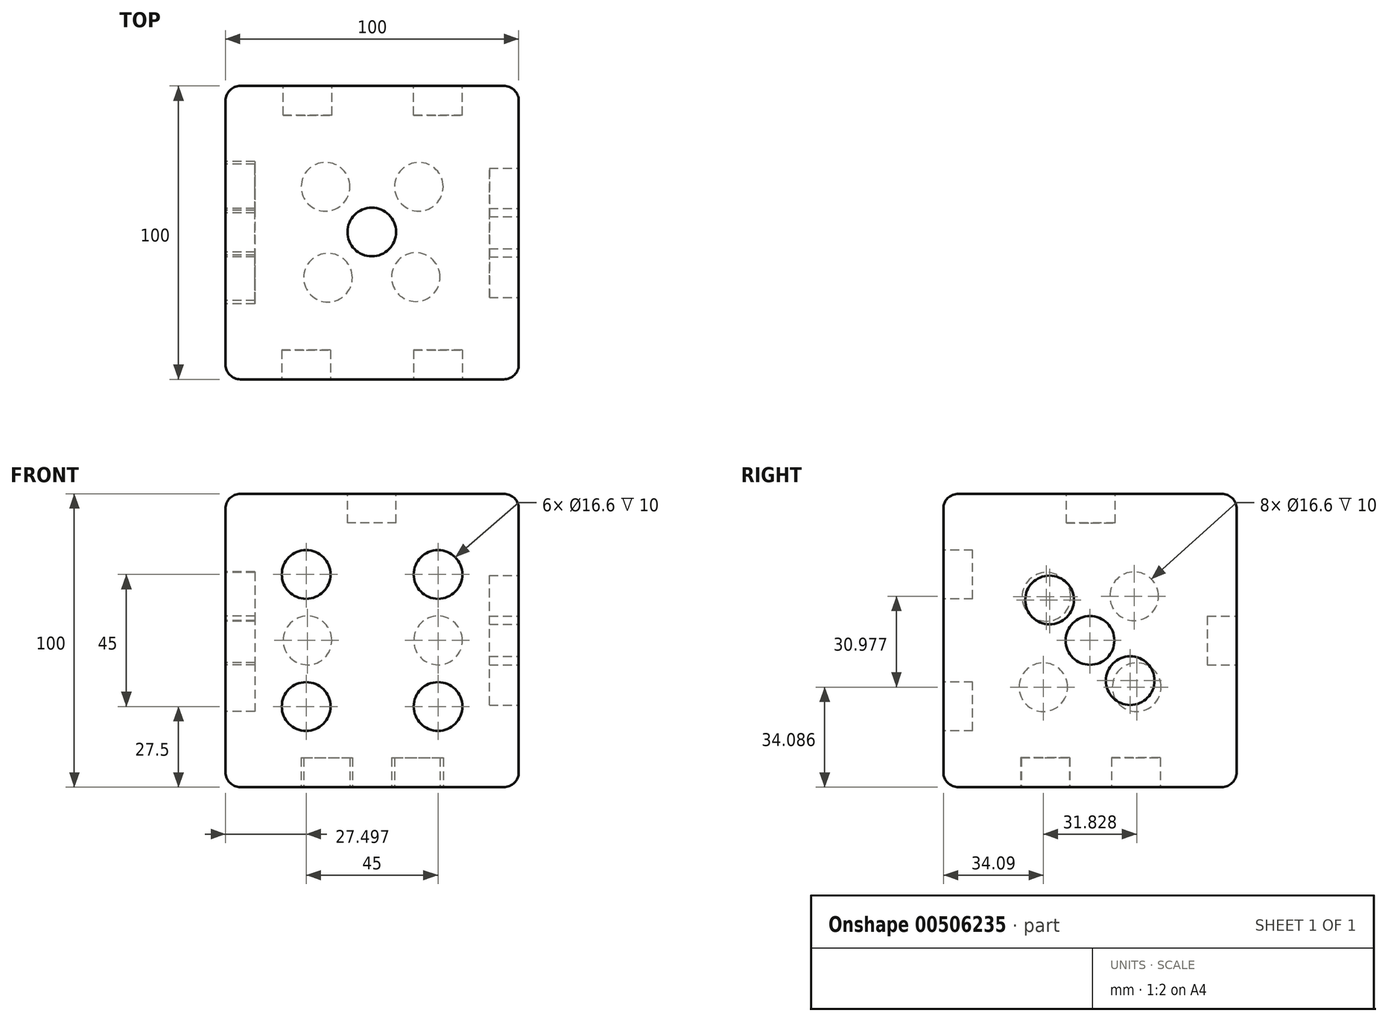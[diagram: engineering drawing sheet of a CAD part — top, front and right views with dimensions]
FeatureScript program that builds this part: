
annotation { "Feature Type Name" : "Feature", "Feature Type Description" : "" }
export const myFeature = defineFeature(function(context is Context, id is Id, definition is map)
    precondition{}
    {
        {
            var Q0;
            Q0=qCreatedBy(makeId("Top.planeOp"),FACE);
            var sketch = newSketch(context, id + "F0", { "sketchPlane" : qUnion([Q0])});
            skLineSegment(sketch, "E0.bottom", {"start": v(-61.95, 62.53) * mm, "end": v(38.05, 62.53) * mm});
            skLineSegment(sketch, "E0.top", {"start": v(-61.95, -37.47) * mm, "end": v(38.05, -37.47) * mm});
            skLineSegment(sketch, "E0.left", {"start": v(-61.95, 62.53) * mm, "end": v(-61.95, -37.47) * mm});
            skLineSegment(sketch, "E0.right", {"start": v(38.05, 62.53) * mm, "end": v(38.05, -37.47) * mm});
            skSolve(sketch);
        }
        {
            var Q0;
            Q0=makeQuery(id+"F0.imprint","IMPRINT",FACE,{"disambiguationData":[TD([[makeQuery(id+"F0.imprint","IMPRINT",EDGE,{"derivedFrom":sQuery(id+"F0.wireOp",EDGE,"E0.bottom")}),-1.0]])]});
            extrude(context, id + "F1", {"entities" : qUnion([Q0]), "depth" : 100 * mm, "offsetDistance" : 25 * mm});
        }
        {
            var Q0;
            Q0=makeQuery(id+"F1.opExtrude","CAP_EDGE",EDGE,{"disambiguationData":[OSD([sQuery(id+"F0.wireOp",EDGE,"E0.top")])],"isStart":false});
            fillet(context, id + "F2", {"entities" : qUnion([Q0]), "radius" : 5.08 * mm, "tangentPropagation" : true, "allowEdgeOverflow" : false});
        }
        {
            var Q0;
            Q0=makeQuery(id+"F1.opExtrude","CAP_EDGE",EDGE,{"disambiguationData":[OSD([sQuery(id+"F0.wireOp",EDGE,"E0.top")])],"isStart":true});
            var Q1;
            Q1=makeQuery(id+"F1.opExtrude","SWEPT_EDGE",EDGE,{"disambiguationData":[OSD([sQuery(id+"F0.wireOp",EDGE,"E0.top"),sQuery(id+"F0.wireOp",EDGE,"E0.right")])]});
            var Q2;
            Q2=makeQuery(id+"F1.opExtrude","SWEPT_EDGE",EDGE,{"disambiguationData":[OSD([sQuery(id+"F0.wireOp",EDGE,"E0.top"),sQuery(id+"F0.wireOp",EDGE,"E0.left")])]});
            var Q3;
            Q3=makeQuery(id+"F1.opExtrude","CAP_EDGE",EDGE,{"disambiguationData":[OSD([sQuery(id+"F0.wireOp",EDGE,"E0.bottom")])],"isStart":false});
            var Q4;
            Q4=makeQuery(id+"F1.opExtrude","CAP_EDGE",EDGE,{"disambiguationData":[OSD([sQuery(id+"F0.wireOp",EDGE,"E0.left")])],"isStart":false});
            var Q5;
            Q5=makeQuery(id+"F1.opExtrude","CAP_EDGE",EDGE,{"disambiguationData":[OSD([sQuery(id+"F0.wireOp",EDGE,"E0.right")])],"isStart":false});
            var Q6;
            Q6=makeQuery(id+"F1.opExtrude","CAP_EDGE",EDGE,{"disambiguationData":[OSD([sQuery(id+"F0.wireOp",EDGE,"E0.right")])],"isStart":true});
            var Q7;
            Q7=makeQuery(id+"F1.opExtrude","SWEPT_EDGE",EDGE,{"disambiguationData":[OSD([sQuery(id+"F0.wireOp",EDGE,"E0.bottom"),sQuery(id+"F0.wireOp",EDGE,"E0.right")])]});
            fillet(context, id + "F3", {"entities" : qUnion([Q0, Q1, Q2, Q3, Q4, Q5, Q6, Q7]), "radius" : 5.08 * mm, "tangentPropagation" : true, "allowEdgeOverflow" : false});
        }
        {
            var Q0;
            Q0=makeQuery(id+"F1.opExtrude","CAP_EDGE",EDGE,{"disambiguationData":[OSD([sQuery(id+"F0.wireOp",EDGE,"E0.bottom")])],"isStart":true});
            var Q1;
            Q1=makeQuery(id+"F1.opExtrude","CAP_EDGE",EDGE,{"disambiguationData":[OSD([sQuery(id+"F0.wireOp",EDGE,"E0.left")])],"isStart":true});
            var Q2;
            {var subQ0=sQuery(id+"F0.wireOp",EDGE,"E0.top");Q2=makeQuery(id+"F3.opFillet","BLEND_EDGE",EDGE,{"blendedFrom":[makeQuery(id+"F1.opExtrude","CAP_EDGE",EDGE,{"disambiguationData":[OSD([subQ0])],"isStart":true}),makeQuery(id+"F1.opExtrude","CAP_FACE",FACE,{"disambiguationData":[OSD([sQuery(id+"F0.wireOp",EDGE,"E0.bottom"),subQ0,sQuery(id+"F0.wireOp",EDGE,"E0.left"),sQuery(id+"F0.wireOp",EDGE,"E0.right")])],"isStart":true})],"blendedInto":[makeQuery(id+"F1.opExtrude","CAP_FACE",FACE,{"disambiguationData":[OSD([sQuery(id+"F0.wireOp",EDGE,"E0.bottom"),subQ0,sQuery(id+"F0.wireOp",EDGE,"E0.left"),sQuery(id+"F0.wireOp",EDGE,"E0.right")])],"isStart":true})]});}
            var Q3;
            {var subQ0=sQuery(id+"F0.wireOp",EDGE,"E0.right");Q3=makeQuery(id+"F3.opFillet","BLEND_EDGE",EDGE,{"blendedFrom":[makeQuery(id+"F1.opExtrude","CAP_EDGE",EDGE,{"disambiguationData":[OSD([subQ0])],"isStart":true}),makeQuery(id+"F1.opExtrude","CAP_FACE",FACE,{"disambiguationData":[OSD([sQuery(id+"F0.wireOp",EDGE,"E0.bottom"),sQuery(id+"F0.wireOp",EDGE,"E0.top"),sQuery(id+"F0.wireOp",EDGE,"E0.left"),subQ0])],"isStart":true})],"blendedInto":[makeQuery(id+"F1.opExtrude","CAP_FACE",FACE,{"disambiguationData":[OSD([sQuery(id+"F0.wireOp",EDGE,"E0.bottom"),sQuery(id+"F0.wireOp",EDGE,"E0.top"),sQuery(id+"F0.wireOp",EDGE,"E0.left"),subQ0])],"isStart":true})]});}
            fillet(context, id + "F4", {"entities" : qUnion([Q0, Q1, Q2, Q3]), "radius" : 5.08 * mm, "tangentPropagation" : true, "allowEdgeOverflow" : false});
        }
        {
            var Q0;
            Q0=makeQuery(id+"F1.opExtrude","SWEPT_EDGE",EDGE,{"disambiguationData":[OSD([sQuery(id+"F0.wireOp",EDGE,"E0.bottom"),sQuery(id+"F0.wireOp",EDGE,"E0.left")])]});
            fillet(context, id + "F5", {"entities" : qUnion([Q0]), "radius" : 5.08 * mm, "tangentPropagation" : true, "allowEdgeOverflow" : false});
        }
        {
            var Q0;
            Q0=makeQuery(id+"F1.opExtrude","CAP_FACE",FACE,{"disambiguationData":[OSD([sQuery(id+"F0.wireOp",EDGE,"E0.bottom"),sQuery(id+"F0.wireOp",EDGE,"E0.top"),sQuery(id+"F0.wireOp",EDGE,"E0.left"),sQuery(id+"F0.wireOp",EDGE,"E0.right")])],"isStart":false});
            var sketch = newSketch(context, id + "F6", { "sketchPlane" : qUnion([Q0])});
            skLineSegment(sketch, "E1", {"start": v(-56.87, 12.53) * mm, "end": v(32.97, 12.53) * mm});
            skLineSegment(sketch, "E2", {"start": v(-11.95, -32.39) * mm, "end": v(-11.95, 57.45) * mm});
            skSolve(sketch);
        }
        {
            var Q0;
            {var subQ0=sQuery(id+"F6.wireOp",EDGE,"E1");var subQ6=sQuery(id+"F6.wireOp",EDGE,"E2");var subQ7=makeQuery(id+"F6.imprint","INTERSECT",VERTEX,{"derivedFrom":[subQ0,subQ6]});Q0=makeQuery(id+"F6.imprint","IMPRINT",FACE,{"disambiguationData":[TD([[makeQuery(id+"F6.imprint","IMPRINT",EDGE,{"disambiguationData":[TD([[subQ7,1.0]])],"derivedFrom":subQ0}),1.0]])]});}
            var sketch = newSketch(context, id + "F7", { "sketchPlane" : qUnion([Q0])});
            skCircle(sketch, "E3", {"center": v(-12.05, 12.77) * mm, "radius": 8.3 * mm});
            skSolve(sketch);
        }
        {
            var Q0;
            {var subQ0=sQuery(id+"F7.wireOp",EDGE,"E3");var subQ1=sQuery(id+"F6.wireOp",EDGE,"E1");var subQ5=sQuery(id+"F6.wireOp",EDGE,"E2");var subQ6=makeQuery(id+"F6.imprint","INTERSECT",VERTEX,{"derivedFrom":[subQ1,subQ5]});var subQ7=makeQuery(id+"F6.imprint","IMPRINT",EDGE,{"disambiguationData":[TD([[subQ6,1.0]])],"derivedFrom":subQ1});var subQ8=makeQuery(id+"F7.imprint","INTERSECT",VERTEX,{"derivedFrom":[subQ7,subQ0]});Q0=makeQuery(id+"F7.imprint","IMPRINT",FACE,{"disambiguationData":[TD([[makeQuery(id+"F7.imprint","IMPRINT",EDGE,{"disambiguationData":[TD([[subQ8,1.0]])],"derivedFrom":subQ0}),1.0]])]});}
            var Q1;
            {var subQ0=sQuery(id+"F7.wireOp",EDGE,"E3");var subQ1=sQuery(id+"F6.wireOp",EDGE,"E1");var subQ5=sQuery(id+"F6.wireOp",EDGE,"E2");var subQ6=makeQuery(id+"F6.imprint","INTERSECT",VERTEX,{"derivedFrom":[subQ1,subQ5]});var subQ7=makeQuery(id+"F6.imprint","IMPRINT",EDGE,{"disambiguationData":[TD([[subQ6,1.0]])],"derivedFrom":subQ1});var subQ8=makeQuery(id+"F7.imprint","INTERSECT",VERTEX,{"derivedFrom":[subQ7,subQ0]});Q1=makeQuery(id+"F7.imprint","IMPRINT",FACE,{"disambiguationData":[TD([[makeQuery(id+"F7.imprint","IMPRINT",EDGE,{"disambiguationData":[TD([[subQ8,-1.0]])],"derivedFrom":subQ0}),1.0]])]});}
            var Q2;
            Q2=sQuery(id+"F7.wireOp",EDGE,"E3");
            extrude(context, id + "F8", {"entities" : qUnion([Q0, Q1]), "operationType" : NewBodyOperationType.REMOVE, "surfaceEntities" : qUnion([Q2]), "oppositeDirection" : true, "depth" : 10 * mm, "offsetDistance" : 25 * mm});
        }
        {
            var Q0;
            Q0=makeQuery(id+"F1.opExtrude","SWEPT_FACE",FACE,{"disambiguationData":[OSD([sQuery(id+"F0.wireOp",EDGE,"E0.left")])]});
            var sketch = newSketch(context, id + "F9", { "sketchPlane" : qUnion([Q0])});
            skCircle(sketch, "E4", {"center": v(-27.6, 65.06) * mm, "radius": 8.3 * mm});
            skCircle(sketch, "E5", {"center": v(-28.45, 34.09) * mm, "radius": 8.3 * mm});
            skCircle(sketch, "E6", {"center": v(3.38, 34.09) * mm, "radius": 8.3 * mm});
            skCircle(sketch, "E7", {"center": v(2.34, 64.88) * mm, "radius": 8.3 * mm});
            skCircle(sketch, "E8", {"center": v(-12.53, 50) * mm, "radius": 8.3 * mm});
            skSolve(sketch);
        }
        {
            var Q0;
            Q0=makeQuery(id+"F1.opExtrude","SWEPT_FACE",FACE,{"disambiguationData":[OSD([sQuery(id+"F0.wireOp",EDGE,"E0.bottom")])]});
            var sketch = newSketch(context, id + "F10", { "sketchPlane" : qUnion([Q0])});
            skCircle(sketch, "E9", {"center": v(-10.55, 50) * mm, "radius": 8.3 * mm});
            skCircle(sketch, "E10", {"center": v(33.98, 50) * mm, "radius": 8.3 * mm});
            skSolve(sketch);
        }
        {
            var Q0;
            Q0=makeQuery(id+"F10.imprint","IMPRINT",FACE,{"disambiguationData":[TD([[makeQuery(id+"F10.imprint","IMPRINT",EDGE,{"derivedFrom":sQuery(id+"F10.wireOp",EDGE,"E9")}),1.0]])]});
            var Q1;
            Q1=makeQuery(id+"F10.imprint","IMPRINT",FACE,{"disambiguationData":[TD([[makeQuery(id+"F10.imprint","IMPRINT",EDGE,{"derivedFrom":sQuery(id+"F10.wireOp",EDGE,"E10")}),1.0]])]});
            var Q2;
            Q2=sQuery(id+"F10.wireOp",EDGE,"E9");
            var Q3;
            Q3=sQuery(id+"F10.wireOp",EDGE,"E10");
            extrude(context, id + "F11", {"entities" : qUnion([Q0, Q1]), "operationType" : NewBodyOperationType.REMOVE, "surfaceEntities" : qUnion([Q2, Q3]), "oppositeDirection" : true, "depth" : 10 * mm, "offsetDistance" : 25 * mm});
        }
        {
            var Q0;
            Q0=makeQuery(id+"F1.opExtrude","CAP_FACE",FACE,{"disambiguationData":[OSD([sQuery(id+"F0.wireOp",EDGE,"E0.bottom"),sQuery(id+"F0.wireOp",EDGE,"E0.top"),sQuery(id+"F0.wireOp",EDGE,"E0.left"),sQuery(id+"F0.wireOp",EDGE,"E0.right")])],"isStart":true});
            var sketch = newSketch(context, id + "F12", { "sketchPlane" : qUnion([Q0])});
            skCircle(sketch, "E11", {"center": v(-26.99, 2.81) * mm, "radius": 8.3 * mm});
            skCircle(sketch, "E12", {"center": v(-27.84, -28.16) * mm, "radius": 8.3 * mm});
            skCircle(sketch, "E13", {"center": v(3.99, -28.16) * mm, "radius": 8.3 * mm});
            skCircle(sketch, "E14", {"center": v(2.95, 2.63) * mm, "radius": 8.3 * mm});
            skSolve(sketch);
        }
        {
            var Q0;
            Q0=makeQuery(id+"F12.imprint","IMPRINT",FACE,{"disambiguationData":[TD([[makeQuery(id+"F12.imprint","IMPRINT",EDGE,{"derivedFrom":sQuery(id+"F12.wireOp",EDGE,"E11")}),1.0]])]});
            var Q1;
            Q1=makeQuery(id+"F12.imprint","IMPRINT",FACE,{"disambiguationData":[TD([[makeQuery(id+"F12.imprint","IMPRINT",EDGE,{"derivedFrom":sQuery(id+"F12.wireOp",EDGE,"E14")}),1.0]])]});
            var Q2;
            Q2=makeQuery(id+"F12.imprint","IMPRINT",FACE,{"disambiguationData":[TD([[makeQuery(id+"F12.imprint","IMPRINT",EDGE,{"derivedFrom":sQuery(id+"F12.wireOp",EDGE,"E13")}),1.0]])]});
            var Q3;
            Q3=makeQuery(id+"F12.imprint","IMPRINT",FACE,{"disambiguationData":[TD([[makeQuery(id+"F12.imprint","IMPRINT",EDGE,{"derivedFrom":sQuery(id+"F12.wireOp",EDGE,"E12")}),1.0]])]});
            var Q4;
            Q4=sQuery(id+"F12.wireOp",EDGE,"E11");
            var Q5;
            Q5=sQuery(id+"F12.wireOp",EDGE,"E14");
            var Q6;
            Q6=sQuery(id+"F12.wireOp",EDGE,"E12");
            var Q7;
            Q7=sQuery(id+"F12.wireOp",EDGE,"E13");
            extrude(context, id + "F13", {"entities" : qUnion([Q0, Q1, Q2, Q3]), "operationType" : NewBodyOperationType.REMOVE, "surfaceEntities" : qUnion([Q4, Q5, Q6, Q7]), "oppositeDirection" : true, "depth" : 10 * mm, "offsetDistance" : 25 * mm});
        }
        {
            var Q0;
            Q0=makeQuery(id+"F9.imprint","IMPRINT",FACE,{"disambiguationData":[TD([[makeQuery(id+"F9.imprint","IMPRINT",EDGE,{"derivedFrom":sQuery(id+"F9.wireOp",EDGE,"E4")}),1.0]])]});
            var Q1;
            Q1=makeQuery(id+"F9.imprint","IMPRINT",FACE,{"disambiguationData":[TD([[makeQuery(id+"F9.imprint","IMPRINT",EDGE,{"derivedFrom":sQuery(id+"F9.wireOp",EDGE,"E8")}),1.0]])]});
            var Q2;
            Q2=makeQuery(id+"F9.imprint","IMPRINT",FACE,{"disambiguationData":[TD([[makeQuery(id+"F9.imprint","IMPRINT",EDGE,{"derivedFrom":sQuery(id+"F9.wireOp",EDGE,"E7")}),1.0]])]});
            var Q3;
            Q3=makeQuery(id+"F9.imprint","IMPRINT",FACE,{"disambiguationData":[TD([[makeQuery(id+"F9.imprint","IMPRINT",EDGE,{"derivedFrom":sQuery(id+"F9.wireOp",EDGE,"E6")}),1.0]])]});
            var Q4;
            Q4=makeQuery(id+"F9.imprint","IMPRINT",FACE,{"disambiguationData":[TD([[makeQuery(id+"F9.imprint","IMPRINT",EDGE,{"derivedFrom":sQuery(id+"F9.wireOp",EDGE,"E5")}),1.0]])]});
            extrude(context, id + "F14", {"entities" : qUnion([Q0, Q1, Q2, Q3, Q4]), "operationType" : NewBodyOperationType.REMOVE, "oppositeDirection" : true, "depth" : 10 * mm, "offsetDistance" : 25 * mm});
        }
        {
            var Q0;
            Q0=makeQuery(id+"F1.opExtrude","SWEPT_FACE",FACE,{"disambiguationData":[OSD([sQuery(id+"F0.wireOp",EDGE,"E0.right")])]});
            var sketch = newSketch(context, id + "F15", { "sketchPlane" : qUnion([Q0])});
            skCircle(sketch, "E15", {"center": v(26.23, 36.3) * mm, "radius": 8.3 * mm});
            skCircle(sketch, "E16", {"center": v(12.53, 50) * mm, "radius": 8.3 * mm});
            skCircle(sketch, "E17", {"center": v(-1.26, 63.8) * mm, "radius": 8.3 * mm});
            skSolve(sketch);
        }
        {
            var Q0;
            Q0=makeQuery(id+"F15.imprint","IMPRINT",FACE,{"disambiguationData":[TD([[makeQuery(id+"F15.imprint","IMPRINT",EDGE,{"derivedFrom":sQuery(id+"F15.wireOp",EDGE,"E15")}),1.0]])]});
            var Q1;
            Q1=makeQuery(id+"F15.imprint","IMPRINT",FACE,{"disambiguationData":[TD([[makeQuery(id+"F15.imprint","IMPRINT",EDGE,{"derivedFrom":sQuery(id+"F15.wireOp",EDGE,"E16")}),1.0]])]});
            var Q2;
            Q2=makeQuery(id+"F15.imprint","IMPRINT",FACE,{"disambiguationData":[TD([[makeQuery(id+"F15.imprint","IMPRINT",EDGE,{"derivedFrom":sQuery(id+"F15.wireOp",EDGE,"E17")}),1.0]])]});
            var Q3;
            Q3=sQuery(id+"F15.wireOp",EDGE,"E15");
            extrude(context, id + "F16", {"entities" : qUnion([Q0, Q1, Q2]), "operationType" : NewBodyOperationType.REMOVE, "surfaceEntities" : qUnion([Q3]), "oppositeDirection" : true, "depth" : 10 * mm, "offsetDistance" : 25 * mm});
        }
        {
            var Q0;
            Q0=makeQuery(id+"F1.opExtrude","SWEPT_FACE",FACE,{"disambiguationData":[OSD([sQuery(id+"F0.wireOp",EDGE,"E0.top")])]});
            var sketch = newSketch(context, id + "F17", { "sketchPlane" : qUnion([Q0])});
            skLineSegment(sketch, "E18", {"start": v(32.97, 94.92) * mm, "end": v(10.55, 94.92) * mm});
            skLineSegment(sketch, "E19", {"start": v(-56.87, 94.92) * mm, "end": v(-34.45, 94.92) * mm});
            skCircle(sketch, "E20", {"center": v(10.55, 27.5) * mm, "radius": 8.3 * mm});
            skCircle(sketch, "E21", {"center": v(-34.45, 27.5) * mm, "radius": 8.3 * mm});
            skCircle(sketch, "E22", {"center": v(10.55, 72.5) * mm, "radius": 8.3 * mm});
            skCircle(sketch, "E23", {"center": v(-34.45, 72.5) * mm, "radius": 8.3 * mm});
            skSolve(sketch);
        }
        {
            var Q0;
            Q0=makeQuery(id+"F17.imprint","IMPRINT",FACE,{"disambiguationData":[TD([[makeQuery(id+"F17.imprint","IMPRINT",EDGE,{"derivedFrom":sQuery(id+"F17.wireOp",EDGE,"E20")}),1.0]])]});
            var Q1;
            Q1=makeQuery(id+"F17.imprint","IMPRINT",FACE,{"disambiguationData":[TD([[makeQuery(id+"F17.imprint","IMPRINT",EDGE,{"derivedFrom":sQuery(id+"F17.wireOp",EDGE,"E22")}),1.0]])]});
            var Q2;
            Q2=makeQuery(id+"F17.imprint","IMPRINT",FACE,{"disambiguationData":[TD([[makeQuery(id+"F17.imprint","IMPRINT",EDGE,{"derivedFrom":sQuery(id+"F17.wireOp",EDGE,"E23")}),1.0]])]});
            var Q3;
            Q3=makeQuery(id+"F17.imprint","IMPRINT",FACE,{"disambiguationData":[TD([[makeQuery(id+"F17.imprint","IMPRINT",EDGE,{"derivedFrom":sQuery(id+"F17.wireOp",EDGE,"E21")}),1.0]])]});
            extrude(context, id + "F18", {"entities" : qUnion([Q0, Q1, Q2, Q3]), "operationType" : NewBodyOperationType.REMOVE, "oppositeDirection" : true, "depth" : 10 * mm, "offsetDistance" : 25 * mm});
        }
    });
